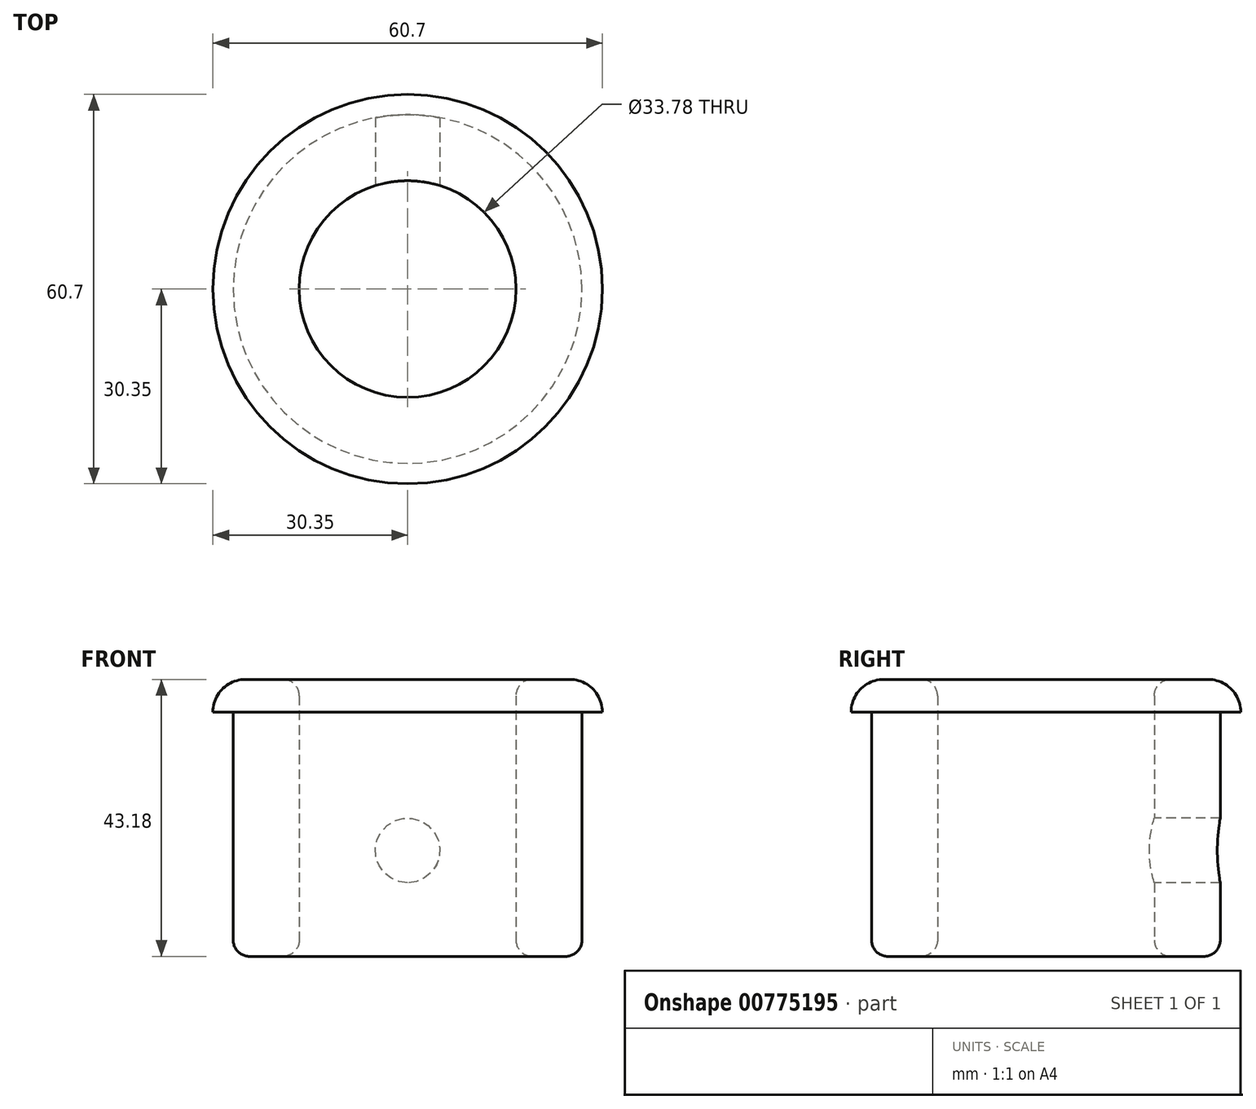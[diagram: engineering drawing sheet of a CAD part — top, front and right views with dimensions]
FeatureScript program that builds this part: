
annotation { "Feature Type Name" : "Feature", "Feature Type Description" : "" }
export const myFeature = defineFeature(function(context is Context, id is Id, definition is map)
    precondition{}
    {
        {
            var Q0;
            Q0=qCreatedBy(makeId("Top.planeOp"),FACE);
            var sketch = newSketch(context, id + "F0", { "sketchPlane" : qUnion([Q0])});
            skCircle(sketch, "E0", {"center": v(0, 0) * mm, "radius": 16.9 * mm});
            skCircle(sketch, "E1", {"center": v(0, 0) * mm, "radius": 27.18 * mm});
            skSolve(sketch);
        }
        {
            var Q0;
            Q0=makeQuery(id+"F0.imprint","IMPRINT",FACE,{"disambiguationData":[TD([[makeQuery(id+"F0.imprint","IMPRINT",EDGE,{"derivedFrom":sQuery(id+"F0.wireOp",EDGE,"E0")}),-1.0]])]});
            extrude(context, id + "F1", {"entities" : qUnion([Q0]), "depth" : 38.1 * mm, "offsetDistance" : 25.4 * mm});
        }
        {
            var Q0;
            Q0=makeQuery(id+"F1.opExtrude","CAP_FACE",FACE,{"disambiguationData":[OSD([sQuery(id+"F0.wireOp",EDGE,"E0"),sQuery(id+"F0.wireOp",EDGE,"E1")])],"isStart":false});
            var sketch = newSketch(context, id + "F2", { "sketchPlane" : qUnion([Q0])});
            skCircle(sketch, "E2", {"center": v(0, 0) * mm, "radius": 30.35 * mm});
            skSolve(sketch);
        }
        {
            var Q0;
            Q0=makeQuery(id+"F2.imprint","IMPRINT",FACE,{"disambiguationData":[TD([[makeQuery(id+"F2.imprint","IMPRINT",EDGE,{"derivedFrom":sQuery(id+"F2.wireOp",EDGE,"E2")}),1.0]])]});
            var Q1;
            Q1=makeQuery(id+"F2.imprint","IMPRINT",FACE,{"disambiguationData":[TD([[makeQuery(id+"F2.imprint","IMPRINT",EDGE,{"derivedFrom":makeQuery(id+"F1.opExtrude","CAP_EDGE",EDGE,{"disambiguationData":[OSD([sQuery(id+"F0.wireOp",EDGE,"E0")])],"isStart":false})}),-1.0]])]});
            extrude(context, id + "F3", {"entities" : qUnion([Q0, Q1]), "operationType" : NewBodyOperationType.ADD, "depth" : 5.08 * mm, "offsetDistance" : 25.4 * mm});
        }
        {
            var Q0;
            Q0=qCreatedBy(makeId("Front.planeOp"),FACE);
            var sketch = newSketch(context, id + "F4", { "sketchPlane" : qUnion([Q0])});
            skPoint(sketch, "E3", {"position": v(0, 16.51) * mm});
            skSolve(sketch);
        }
        {
            var Q0;
            Q0=sQuery(id+"F4.wireOp",VERTEX,"E3");
            var Q1;
            Q1=makeQuery(id+"F1.opExtrude","SWEPT_BODY",BODY,{"disambiguationData":[OSD([sQuery(id+"F0.wireOp",EDGE,"E0"),sQuery(id+"F0.wireOp",EDGE,"E1")])]});
            hole(context, id + "F5", {"style" : HoleStyle.SIMPLE, "endStyle" : HoleEndStyle.THROUGH, "standardTappedOrClearance" : lookupTablePath({ "standard" : "ANSI", "fit" : "Normal (ASME)", "size" : "3/8", "type" : "Clearance" }), "standardBlindInLast" : lookupTablePath({ "fit" : "Free", "standard" : "ANSI", "size" : "3/8", "type" : "Clearance" }), "holeDiameter" : 10.08 * mm, "majorDiameter" : 6.35 * mm, "isTappedThrough" : true, "tappedDepth" : 12.7 * mm, "tapClearance" : 3, "locations" : qUnion([Q0]), "scope" : qUnion([Q1])});
        }
        {
            var Q0;
            Q0=makeQuery(id+"F1.opExtrude","CAP_EDGE",EDGE,{"disambiguationData":[OSD([sQuery(id+"F0.wireOp",EDGE,"E0")])],"isStart":true});
            var Q1;
            Q1=makeQuery(id+"F1.opExtrude","CAP_EDGE",EDGE,{"disambiguationData":[OSD([sQuery(id+"F0.wireOp",EDGE,"E1")])],"isStart":true});
            var Q2;
            Q2=makeQuery(id+"F3.opExtrude","CAP_EDGE",EDGE,{"disambiguationData":[OSD([sQuery(id+"F0.wireOp",EDGE,"E0")])],"isStart":false});
            fillet(context, id + "F6", {"entities" : qUnion([Q0, Q1, Q2]), "radius" : 2.54 * mm, "tangentPropagation" : true, "allowEdgeOverflow" : false});
        }
        {
            var Q0;
            Q0=makeQuery(id+"F3.opExtrude","CAP_EDGE",EDGE,{"disambiguationData":[OSD([sQuery(id+"F2.wireOp",EDGE,"E2")])],"isStart":false});
            fillet(context, id + "F7", {"entities" : qUnion([Q0]), "radius" : 5.08 * mm, "tangentPropagation" : true, "allowEdgeOverflow" : false});
        }
    });
